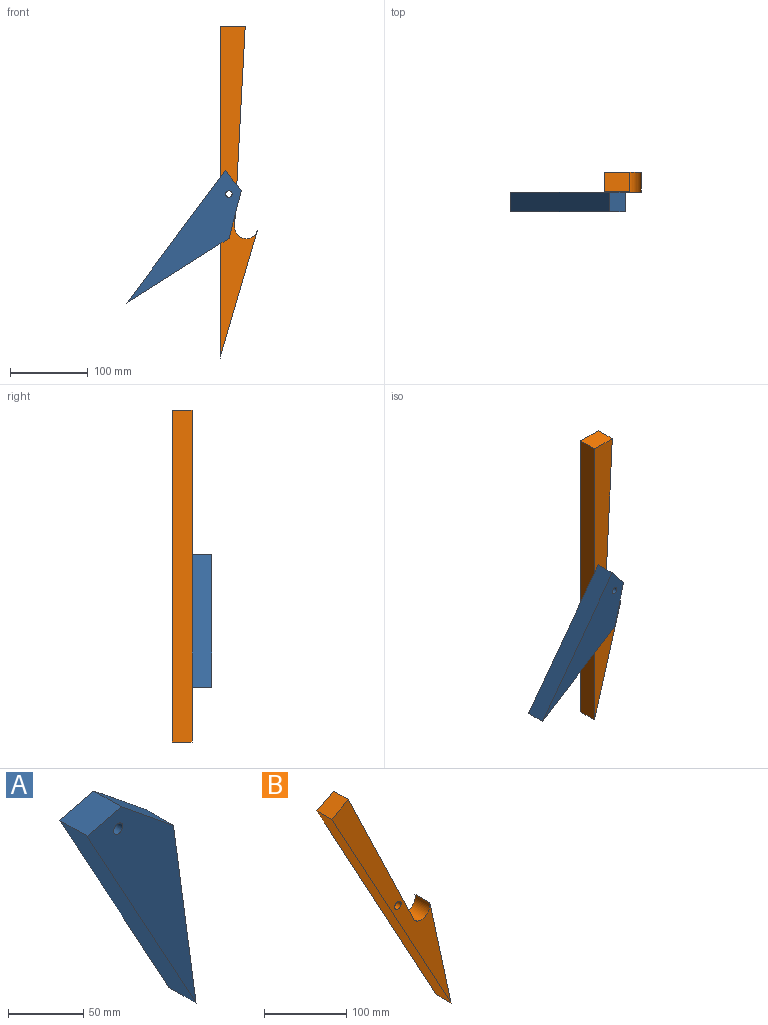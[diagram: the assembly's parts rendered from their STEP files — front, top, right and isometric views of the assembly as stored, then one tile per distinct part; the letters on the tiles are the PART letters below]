
ASSEMBLY  parts=2 mates=1
PART A: 7 faces, bbox 102.2x25.4x194.6 mm
  f0: plane 154.63x25.4mm, normal (0.99,0,0.14), area 3964.4mm2, adj f1,f4,f5,f6
  f1: plane 49.09x39.92mm, normal (0.63,0,0.78), area 1607.2mm2, adj f0,f2,f5,f6
  f2: plane 31.87x25.4mm, normal (-0.24,0,0.97), area 834.8mm2, adj f1,f4,f5,f6
  f3: cylinder r=4.14mm len=25.4mm, axis (0,1,0), area 661.3mm2, adj f5,f6
  f4: plane 186.53x102.17mm, normal (-0.88,0,-0.48), area 5402mm2, adj f0,f2,f5,f6
  f5: plane 194.55x102.17mm, normal (0,-1,0), area 6701.1mm2, adj f0,f1,f2,f3,f4
  f6: plane 194.55x102.17mm, normal (0,1,0), area 6701.1mm2, adj f0,f1,f2,f3,f4
PART B: 8 faces, bbox 204.7x25.4x390.5 mm
  f0: plane 375.06x204.66mm, normal (-0.88,0,-0.48), area 10852.5mm2, adj f1,f4,f6,f7
  f1: plane 167.25x36.49mm, normal (0.98,0,0.21), area 4348mm2, adj f0,f2,f6,f7
  f2: cylinder r=15mm len=28.53mm, axis (0,1,0), area 1108.6mm2, adj f1,f3,f6,f7
  f3: plane 232.98x111.61mm, normal (0.9,0,0.43), area 6561.6mm2, adj f2,f4,f6,f7
  f4: plane 28.39x25.4mm, normal (-0.48,0,0.88), area 821.4mm2, adj f0,f3,f6,f7
  f5: cylinder r=5.53mm len=25.4mm, axis (0,1,0), area 882.3mm2, adj f6,f7
  f6: plane 390.55x204.66mm, normal (0,-1,0), area 10304.1mm2, adj f0,f1,f2,f3,f4,f5
  f7: plane 390.55x204.66mm, normal (0,1,0), area 10304.1mm2, adj f0,f1,f2,f3,f4,f5
PLACE A rot(axis=(0,1,0),65.4deg) t=(-125.54,25.09,42.94)mm
PLACE B rot(axis=(0,1,0),28.6deg) t=(-1.34,25.09,-5.96)mm
MATE revolute B.f5 <-> A.f3  axis (0,-1,0) through (10.03,-0.31,205.06)mm
